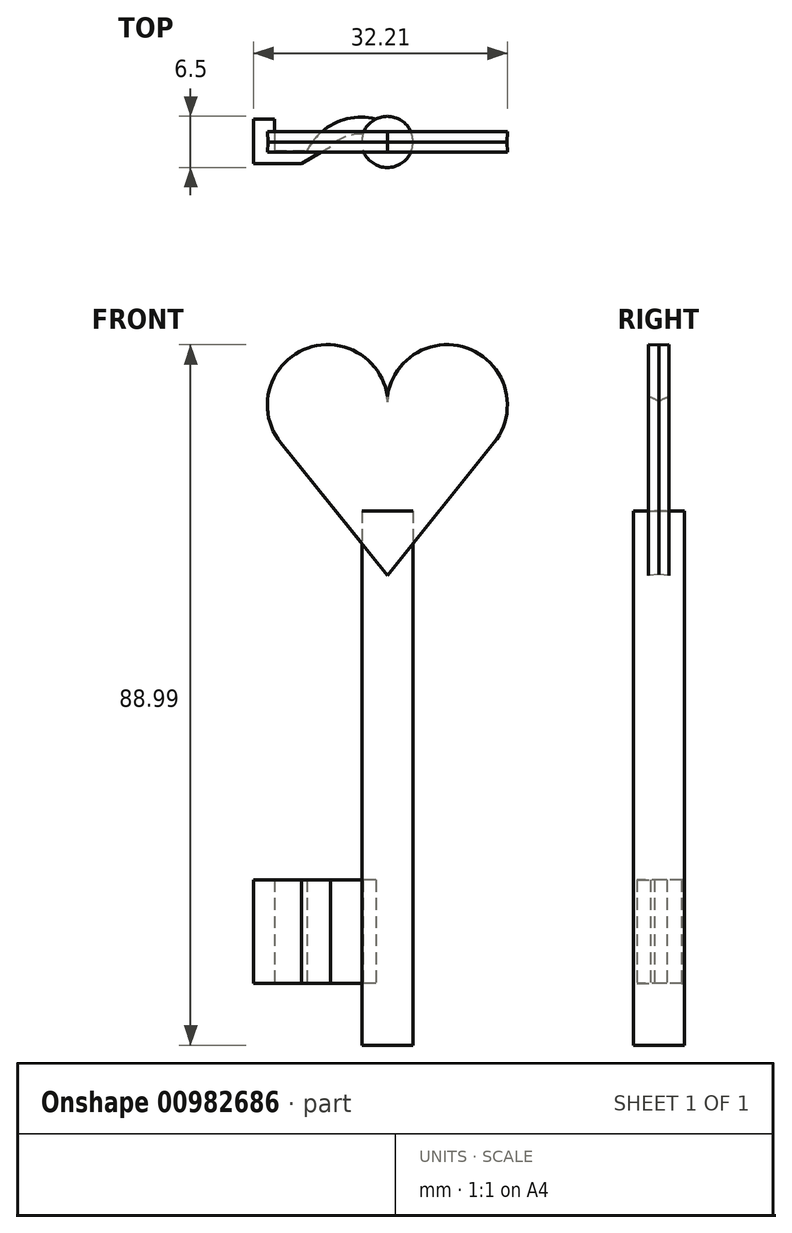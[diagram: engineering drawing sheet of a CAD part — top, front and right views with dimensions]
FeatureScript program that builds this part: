
annotation { "Feature Type Name" : "Feature", "Feature Type Description" : "" }
export const myFeature = defineFeature(function(context is Context, id is Id, definition is map)
    precondition{}
    {
        {
            var Q0;
            Q0=qCreatedBy(makeId("Top.planeOp"),FACE);
            var sketch = newSketch(context, id + "F0", { "sketchPlane" : qUnion([Q0])});
            skLineSegment(sketch, "E0", {"start": v(-16.97, 2.9) * mm, "end": v(-16.97, -2.78) * mm});
            skLineSegment(sketch, "E1", {"start": v(-16.97, -2.78) * mm, "end": v(-10.9, -2.78) * mm});
            skLineSegment(sketch, "E2", {"start": v(-10.9, -2.78) * mm, "end": v(-7.24, -0.58) * mm});
            skArc(sketch, "E3", {"start": v(-3.09, 1.01) * mm, "mid": v(-5.33, 0.65) * mm, "end": v(-7.24, -0.58) * mm});
            skLineSegment(sketch, "E4", {"start": v(-16.97, 2.9) * mm, "end": v(-14.3, 2.9) * mm});
            skLineSegment(sketch, "E5", {"start": v(-14.3, 2.9) * mm, "end": v(-14.3, -1.1) * mm});
            skLineSegment(sketch, "E6", {"start": v(-14.3, -1.1) * mm, "end": v(-10.2, -1.1) * mm});
            skLineSegment(sketch, "E7", {"start": v(-7.24, -0.58) * mm, "end": v(-3.09, 1.01) * mm, "construction": true});
            skArc(sketch, "E8.0", {"start": v(-1.47, 2.9) * mm, "mid": v(-6.54, 2.44) * mm, "end": v(-10.2, -1.1) * mm});
            skLineSegment(sketch, "E9", {"start": v(-14.3, 2.9) * mm, "end": v(-1.47, 2.9) * mm, "construction": true});
            skCircle(sketch, "E10", {"center": v(0, 0) * mm, "radius": 3.25 * mm, "construction": true});
            skLineSegment(sketch, "E11.0", {"start": v(-43.78, 3.25) * mm, "end": v(-41.11, 3.25) * mm, "construction": true});
            skLineSegment(sketch, "E12", {"start": v(-41.11, 3.25) * mm, "end": v(-22.95, 3.25) * mm, "construction": true});
            skLineSegment(sketch, "E13", {"start": v(-1.47, 2.9) * mm, "end": v(-3.09, 1.01) * mm});
            skSolve(sketch);
        }
        {
            var Q0;
            Q0=makeQuery(id+"F0.imprint","IMPRINT",FACE,{"disambiguationData":[TD([[makeQuery(id+"F0.imprint","IMPRINT",EDGE,{"derivedFrom":sQuery(id+"F0.wireOp",EDGE,"E0")}),1.0]])]});
            extrude(context, id + "F1", {"entities" : qUnion([Q0]), "depth" : 13.13 * mm, "offsetDistance" : 25 * mm});
        }
        {
            var Q0;
            Q0=qCreatedBy(makeId("Top.planeOp"),FACE);
            var sketch = newSketch(context, id + "F2", { "sketchPlane" : qUnion([Q0])});
            skCircle(sketch, "E14", {"center": v(0, 0) * mm, "radius": 3.25 * mm});
            skSolve(sketch);
        }
        {
            var Q0;
            Q0=makeQuery(id+"F2.imprint","IMPRINT",FACE,{"disambiguationData":[TD([[makeQuery(id+"F2.imprint","IMPRINT",EDGE,{"derivedFrom":sQuery(id+"F2.wireOp",EDGE,"E14")}),1.0]])]});
            extrude(context, id + "F3", {"entities" : qUnion([Q0]), "operationType" : NewBodyOperationType.ADD, "depth" : 60 * mm, "offsetDistance" : 25 * mm, "hasSecondDirection" : true, "secondDirectionOppositeDirection" : true, "secondDirectionDepth" : 7.85 * mm});
        }
        {
            var Q0;
            Q0=qCreatedBy(makeId("Front.planeOp"),FACE);
            var sketch = newSketch(context, id + "F4", { "sketchPlane" : qUnion([Q0])});
            skLineSegment(sketch, "E15", {"start": v(0, 51.92) * mm, "end": v(13.5, 68.72) * mm});
            skLineSegment(sketch, "E16", {"start": v(0, 51.92) * mm, "end": v(-13.5, 68.72) * mm});
            skArc(sketch, "E17", {"start": v(-13.5, 68.72) * mm, "mid": v(-9.92, 80.7) * mm, "end": v(0, 73.09) * mm});
            skArc(sketch, "E18", {"start": v(13.5, 68.72) * mm, "mid": v(9.92, 80.7) * mm, "end": v(0, 73.09) * mm});
            skLineSegment(sketch, "E19", {"start": v(0, 51.92) * mm, "end": v(0, 60) * mm, "construction": true});
            skLineSegment(sketch, "E20", {"start": v(0, 0) * mm, "end": v(0, 60) * mm, "construction": true});
            skSolve(sketch);
        }
        {
            var Q0;
            Q0 = qSketchRegion(id + "F4", true);
            extrude(context, id + "F5", {"entities" : qUnion([Q0]), "depth" : 1.3 * mm, "offsetDistance" : 25 * mm, "hasDraft" : true, "draftAngle" : 3 * degree, "hasSecondDirection" : true, "secondDirectionOppositeDirection" : true, "secondDirectionDepth" : 1.3 * mm, "hasSecondDirectionDraft" : true, "secondDirectionDraftAngle" : 3 * degree});
        }
    });
